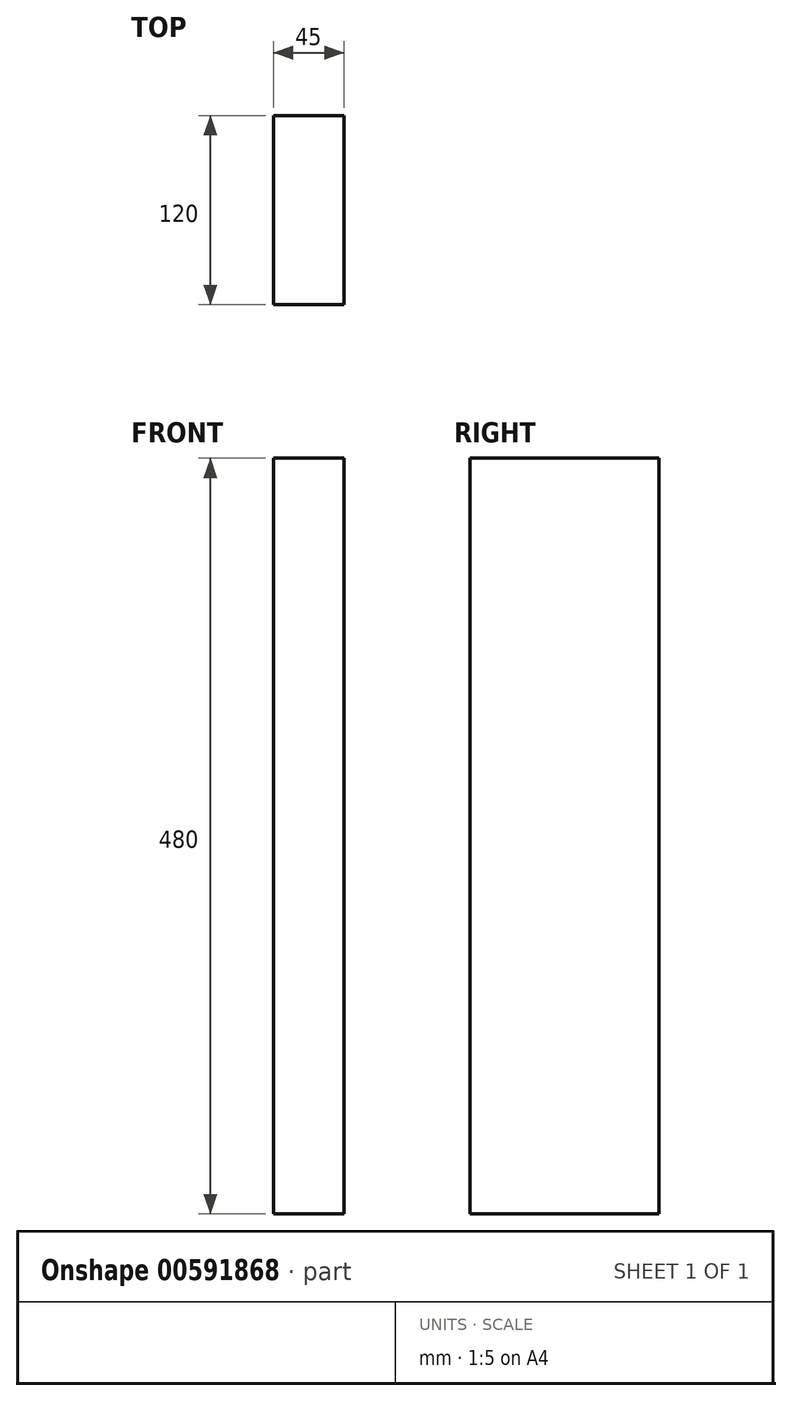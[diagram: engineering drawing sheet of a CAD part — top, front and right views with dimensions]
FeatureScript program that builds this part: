
annotation { "Feature Type Name" : "Feature", "Feature Type Description" : "" }
export const myFeature = defineFeature(function(context is Context, id is Id, definition is map)
    precondition{}
    {
        {
            var Q0;
            Q0=qCreatedBy(makeId("Top.planeOp"),FACE);
            var sketch = newSketch(context, id + "F0", { "sketchPlane" : qUnion([Q0])});
            skLineSegment(sketch, "E0.bottom", {"start": v(0, 0) * mm, "end": v(45, 0) * mm});
            skLineSegment(sketch, "E0.top", {"start": v(0, 120) * mm, "end": v(45, 120) * mm});
            skLineSegment(sketch, "E0.left", {"start": v(0, 0) * mm, "end": v(0, 120) * mm});
            skLineSegment(sketch, "E0.right", {"start": v(45, 0) * mm, "end": v(45, 120) * mm});
            skSolve(sketch);
        }
        {
            var Q0;
            Q0=makeQuery(id+"F0.imprint","IMPRINT",FACE,{"disambiguationData":[TD([[makeQuery(id+"F0.imprint","IMPRINT",EDGE,{"derivedFrom":sQuery(id+"F0.wireOp",EDGE,"E0.bottom")}),1.0]])]});
            extrude(context, id + "F1", {"entities" : qUnion([Q0]), "depth" : 480 * mm, "offsetDistance" : 25 * mm});
        }
    });
